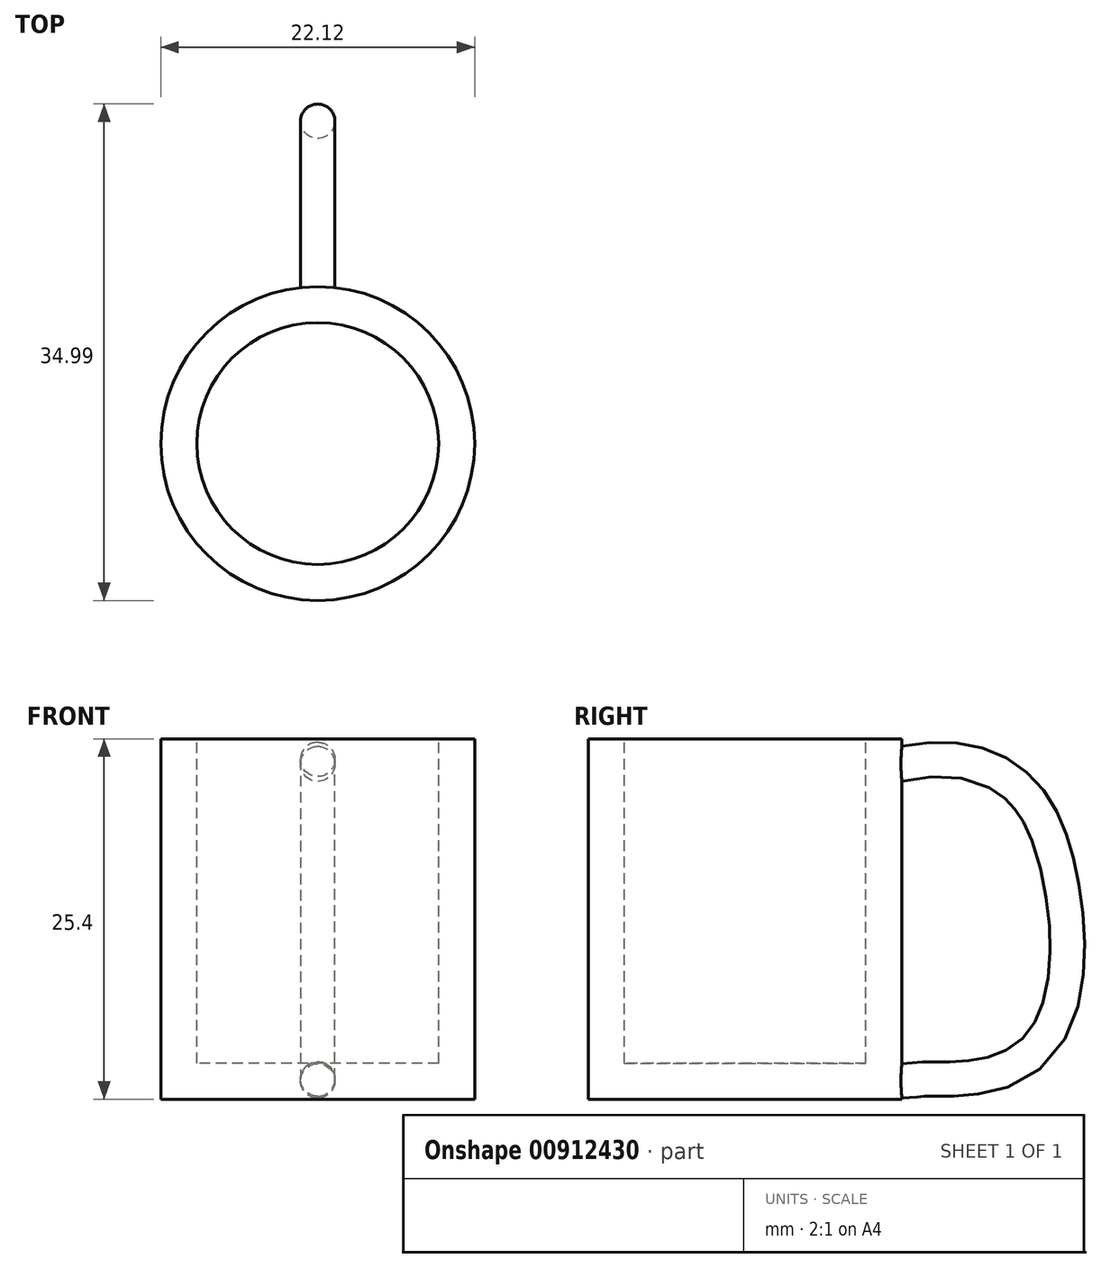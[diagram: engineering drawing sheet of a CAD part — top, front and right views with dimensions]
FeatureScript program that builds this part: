
annotation { "Feature Type Name" : "Feature", "Feature Type Description" : "" }
export const myFeature = defineFeature(function(context is Context, id is Id, definition is map)
    precondition{}
    {
        {
            var Q0;
            Q0=qCreatedBy(makeId("Right.planeOp"),FACE);
            var sketch = newSketch(context, id + "F0", { "sketchPlane" : qUnion([Q0])});
            skLineSegment(sketch, "E0.bottom", {"start": v(0, 34.52) * mm, "end": v(11.06, 34.52) * mm});
            skLineSegment(sketch, "E0.top", {"start": v(0, 9.12) * mm, "end": v(11.06, 9.12) * mm});
            skLineSegment(sketch, "E0.left", {"start": v(0, 34.52) * mm, "end": v(0, 9.12) * mm});
            skLineSegment(sketch, "E0.right", {"start": v(11.06, 34.52) * mm, "end": v(11.06, 9.12) * mm});
            skSolve(sketch);
        }
        {
            var Q0;
            Q0 = qSketchRegion(id + "F0", true);
            var Q1;
            Q1=sQuery(id+"F0.wireOp",EDGE,"E0.left");
            revolve(context, id + "F1", {"surfaceOperationType" : NewSurfaceOperationType.NEW, "entities" : qUnion([Q0]), "axis" : qUnion([Q1]), "revolveType" : RevolveType.FULL});
        }
        {
            var Q0;
            Q0=makeQuery(id+"F1.opRevolve","SWEPT_FACE",FACE,{"disambiguationData":[OSD([sQuery(id+"F0.wireOp",EDGE,"E0.bottom")])]});
            shell(context, id + "F2", {"entities" : qUnion([Q0]), "thickness" : 2.54 * mm});
        }
        {
            var Q0;
            Q0=qCreatedBy(makeId("Right.planeOp"),FACE);
            var sketch = newSketch(context, id + "F3", { "sketchPlane" : qUnion([Q0])});
            skFitSpline(sketch, "E1", {"points": [v(9.84, 29.6) * mm, v(16.76, 29.53) * mm, v(19.25, 25.2) * mm, v(18.49, 14.55) * mm, v(12.58, 13.32) * mm, v(9.7, 13.32) * mm], "startDerivative": vector(49.47, 14.38) * mm, "endDerivative": vector(-32.1, 5.55) * mm});
            skSolve(sketch);
        }
        {
            var Q0;
            Q0=sQuery(id+"F3.wireOp",VERTEX,"E1.end");
            var Q1;
            Q1=sQuery(id+"F3.wireOp",EDGE,"E1");
            cPlane(context, id + "F4", {"entities" : qUnion([Q0, Q1]), "cplaneType" : CPlaneType.CURVE_POINT, "offset" : 25.4 * mm, "width" : 152.4 * mm, "height" : 152.4 * mm});
        }
        {
            var Q0;
            Q0=qCreatedBy(id+"F4.planeOp",FACE);
            var sketch = newSketch(context, id + "F5", { "sketchPlane" : qUnion([Q0])});
            skCircle(sketch, "E2", {"center": v(0, 12) * mm, "radius": 1.21 * mm});
            skSolve(sketch);
        }
        {
            var Q0;
            Q0=makeQuery(id+"F5.imprint","IMPRINT",FACE,{"disambiguationData":[TD([[makeQuery(id+"F5.imprint","IMPRINT",EDGE,{"derivedFrom":sQuery(id+"F5.wireOp",EDGE,"E2")}),1.0]])]});
            var Q1;
            Q1=sQuery(id+"F3.wireOp",EDGE,"E1");
            sweep(context, id + "F6", {"operationType" : NewBodyOperationType.ADD, "profiles" : qUnion([Q0]), "path" : qUnion([Q1])});
        }
    });
